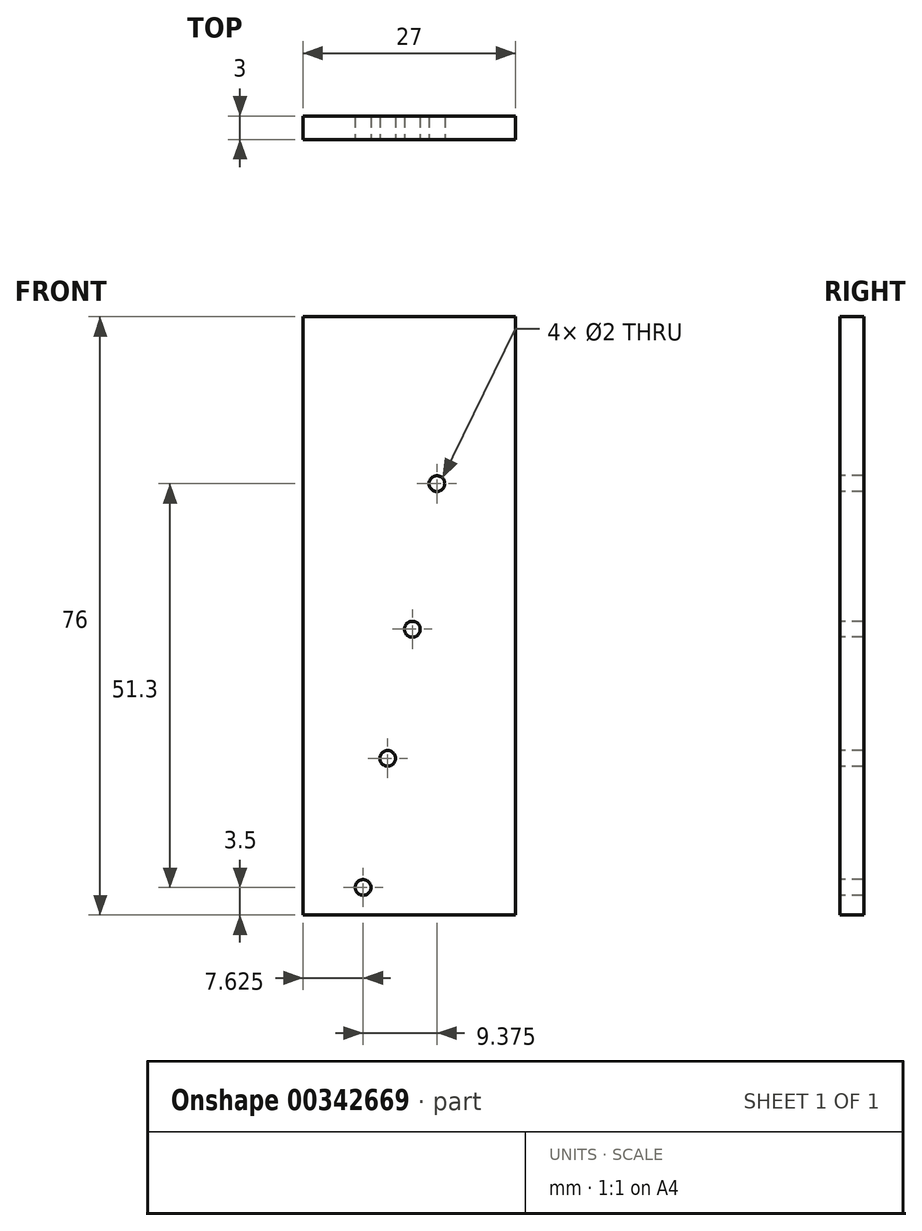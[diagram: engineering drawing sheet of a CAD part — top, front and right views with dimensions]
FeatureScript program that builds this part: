
annotation { "Feature Type Name" : "Feature", "Feature Type Description" : "" }
export const myFeature = defineFeature(function(context is Context, id is Id, definition is map)
    precondition{}
    {
        {
            var Q0;
            Q0=qCreatedBy(makeId("Front.planeOp"),FACE);
            var sketch = newSketch(context, id + "F0", { "sketchPlane" : qUnion([Q0])});
            skLineSegment(sketch, "E0.bottom", {"start": v(0, 0) * mm, "end": v(27, 0) * mm});
            skLineSegment(sketch, "E0.top", {"start": v(0, 76) * mm, "end": v(27, 76) * mm});
            skLineSegment(sketch, "E0.left", {"start": v(0, 0) * mm, "end": v(0, 76) * mm});
            skLineSegment(sketch, "E0.right", {"start": v(27, 0) * mm, "end": v(27, 76) * mm});
            skSolve(sketch);
        }
        {
            var Q0;
            Q0=makeQuery(id+"F0.imprint","IMPRINT",FACE,{"disambiguationData":[TD([[makeQuery(id+"F0.imprint","IMPRINT",EDGE,{"derivedFrom":sQuery(id+"F0.wireOp",EDGE,"E0.bottom")}),1.0]])]});
            extrude(context, id + "F1", {"entities" : qUnion([Q0]), "oppositeDirection" : true, "depth" : 3 * mm});
        }
        {
            var Q0;
            Q0=makeQuery(id+"F1.opExtrude","CAP_FACE",FACE,{"disambiguationData":[OSD([sQuery(id+"F0.wireOp",EDGE,"E0.bottom"),sQuery(id+"F0.wireOp",EDGE,"E0.top"),sQuery(id+"F0.wireOp",EDGE,"E0.left"),sQuery(id+"F0.wireOp",EDGE,"E0.right")])],"isStart":true});
            var sketch = newSketch(context, id + "F2", { "sketchPlane" : qUnion([Q0])});
            skLineSegment(sketch, "E1", {"start": v(7.63, 3.5) * mm, "end": v(7.63, 19.9) * mm, "construction": true});
            skLineSegment(sketch, "E2", {"start": v(7.63, 19.9) * mm, "end": v(10.75, 19.9) * mm, "construction": true});
            skLineSegment(sketch, "E3", {"start": v(10.75, 19.9) * mm, "end": v(10.75, 36.3) * mm, "construction": true});
            skLineSegment(sketch, "E4", {"start": v(10.75, 36.3) * mm, "end": v(13.88, 36.3) * mm, "construction": true});
            skLineSegment(sketch, "E5", {"start": v(13.88, 36.3) * mm, "end": v(13.88, 54.8) * mm, "construction": true});
            skLineSegment(sketch, "E6", {"start": v(13.88, 54.8) * mm, "end": v(17, 54.8) * mm, "construction": true});
            skCircle(sketch, "E7", {"center": v(7.63, 3.5) * mm, "radius": 1 * mm});
            skCircle(sketch, "E8", {"center": v(10.75, 19.9) * mm, "radius": 1 * mm});
            skCircle(sketch, "E9", {"center": v(13.88, 36.3) * mm, "radius": 1 * mm});
            skCircle(sketch, "E10", {"center": v(17, 54.8) * mm, "radius": 1 * mm});
            skSolve(sketch);
        }
        {
            var Q0;
            Q0=makeQuery(id+"F2.imprint","IMPRINT",FACE,{"disambiguationData":[TD([[makeQuery(id+"F2.imprint","IMPRINT",EDGE,{"derivedFrom":sQuery(id+"F2.wireOp",EDGE,"E10")}),1.0]])]});
            var Q1;
            Q1=makeQuery(id+"F2.imprint","IMPRINT",FACE,{"disambiguationData":[TD([[makeQuery(id+"F2.imprint","IMPRINT",EDGE,{"derivedFrom":sQuery(id+"F2.wireOp",EDGE,"E9")}),1.0]])]});
            var Q2;
            Q2=makeQuery(id+"F2.imprint","IMPRINT",FACE,{"disambiguationData":[TD([[makeQuery(id+"F2.imprint","IMPRINT",EDGE,{"derivedFrom":sQuery(id+"F2.wireOp",EDGE,"E8")}),1.0]])]});
            var Q3;
            Q3=makeQuery(id+"F2.imprint","IMPRINT",FACE,{"disambiguationData":[TD([[makeQuery(id+"F2.imprint","IMPRINT",EDGE,{"derivedFrom":sQuery(id+"F2.wireOp",EDGE,"E7")}),1.0]])]});
            var Q4;
            Q4=sQuery(id+"F2.wireOp",EDGE,"E7");
            var Q5;
            Q5=sQuery(id+"F2.wireOp",EDGE,"E8");
            var Q6;
            Q6=sQuery(id+"F2.wireOp",EDGE,"E9");
            var Q7;
            Q7=sQuery(id+"F2.wireOp",EDGE,"E10");
            extrude(context, id + "F3", {"entities" : qUnion([Q0, Q1, Q2, Q3]), "operationType" : NewBodyOperationType.REMOVE, "surfaceEntities" : qUnion([Q4, Q5, Q6, Q7]), "oppositeDirection" : true, "depth" : 3 * mm});
        }
    });
